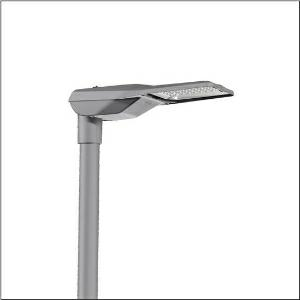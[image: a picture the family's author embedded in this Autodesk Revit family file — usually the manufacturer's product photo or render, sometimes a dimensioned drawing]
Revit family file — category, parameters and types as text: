
# Revit family: streetlight_sl_21_iq_mini___p0_5a_5xe2v31v08gb_1d9f
name_source: partatom
category: Lighting Fixtures
units: mm (PartAtom-declared; Revit-internal decimal feet)

## family parameters
Cut with Voids When Loaded = No
Host = Face
Light Source = No
Part Type = Normal
Room Calculation Point = No
Round Connector Dimension = Use Diameter
Shared = No

## types (1)
- --- (1 x LED, 5880 lm, 39.8 W, 3000K)
    Apparent Load = 40 VA
    CIE Flux Codes = 37 73 96 100 100
    Color Rendering = 70
    Color Temperature = 3000K
    Default Elevation = 1800 mm
    Description = Streetlight SL 21 iQ mini, mast luminaire, primary light control with lens, of PMMA, primary optical cover: cover, of toughened safety glass, transparent, light distribution: P0.5a, light emission: direct distribution, primary light characteristic: asymmetric, installation type: post-top, side-entry, LED, High Power LED, rated luminous flux: 5.880lm, luminous efficacy: 148lm/W, light colour: 730, colour temperature: 3000K, control gear: iQ-Street Remote, D4i with power reduction, control: pre-setting: logarithmic dimming characteristic, Street-Remote, Auto-Match, Temp-Guard, Lumen-Switch, Night-Set, Smart-Wire, Light-Fading, Desk-Remote (wireless, voltage-free reading and setting of iQ features in the workshop via application-optimized NFC function/RFID function), optimised constant luminous flux control (CLO 2.0), mains connection: 220..240V, AC, 50/60Hz, start of lifetime: 40W, end of service life: 41W, reduction: 18W, luminaire housing, of diecast aluminium, powder-coated, Siteco® metallic grey (DB 702S), corrosivity category C5 mid according to DIN EN ISO 12944, please order mast flange separately, inclination adjustable: 0°, 5°, 10°, 15°, sealing non-destructively replaceable, multi-level sealing system, length: 628mm, width: 235mm, height: 110mm, mast flange for spigot size: 42mm (side-entry): 5XC10008XM4, 60/48mm (side-entry/post-top): 5XC10108XM2, 76/60mm (side-entry/post-top): 5XC10108XM1, mounting height: 4..8m, Smart Interface above, protection rating (complete): IP66, insulation class (complete): insulation class II (safety insulation), certification: CE, ENEC, ENEC+, VDE, impact resistance: IK10, permissible operating ambient temperature for outdoor applications: -40..+50°C, standard-compliant lighting for roads and squares, packaging unit: 1 piece

Light Distribution: P0.5a
    Height = 110 mm
    Lamp = 1 x LED
    Lamp Light Flux = 5880 lm
    Lamp Power = 39.8 W
    Lamp count = 1
    Length = 625 mm
    Luminous efficacy = 148 lm/W
    Manufacturer = Siteco
    ModVariant = No
    Model = 5XE2V31V08GB
    Number of Poles = 1
    OnlyDefault = Yes
    Power Factor = 1
    Product Name = Streetlight SL 21 iQ mini | P0.5a
    Product group = mast luminaire | pylon top
    ProductGroupID = 6100
    Protection Class = Protection class II
    Protection Degree = IP 66
    RLX_Detail_Level = 1
    RLX_Emergency_Light_Flux = 0 lm
    RLX_Emergency_Type = 0
    RLX_Emergency_Type_DB = No
    RlxData = <blob elided: 92033 chars, md5=9ae32b71>
    Socket = socket
    Standby Power = 0 W
    System Light Flux = 5880 lm
    System Power = 40 W
    Type Comments = factory setting: luminous flux: 100 % | dim-lin: 254 | 800 mA
    Type Image = l_1003515.jpg
    URL = http://relux.com
    VarID = @adj_092195
    Voltage = 0 V
    Weight = 0.00 kg
    Width = 234 mm

## geometry (parser evidence)
native form markers: Blend x4, Sweep x12
no freeform markers — native parametric forms only
